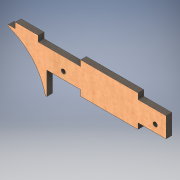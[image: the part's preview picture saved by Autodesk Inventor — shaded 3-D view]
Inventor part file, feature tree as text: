
AUTODESK INVENTOR PART (.ipt)
format: ipt  version: 2019 (Build 230136000, 136)  size: 154,624 bytes
history: native  units: mm
features: extrude x2, sketch x2, other x1
ambient origin geometry x8: Origin, YZ Plane, XZ Plane, XY Plane, X Axis, Y Axis, Z Axis, Center Point
bodies: Body1 (feature_tree)
feature tree (5):
  other  "Твердое тело1"
  extrude  "Выдавливание1"  Depth=14.0mm
  extrude  "Выдавливание2"  Depth=4.0mm
  sketch  "Эскиз1"
  sketch  "Эскиз2"
